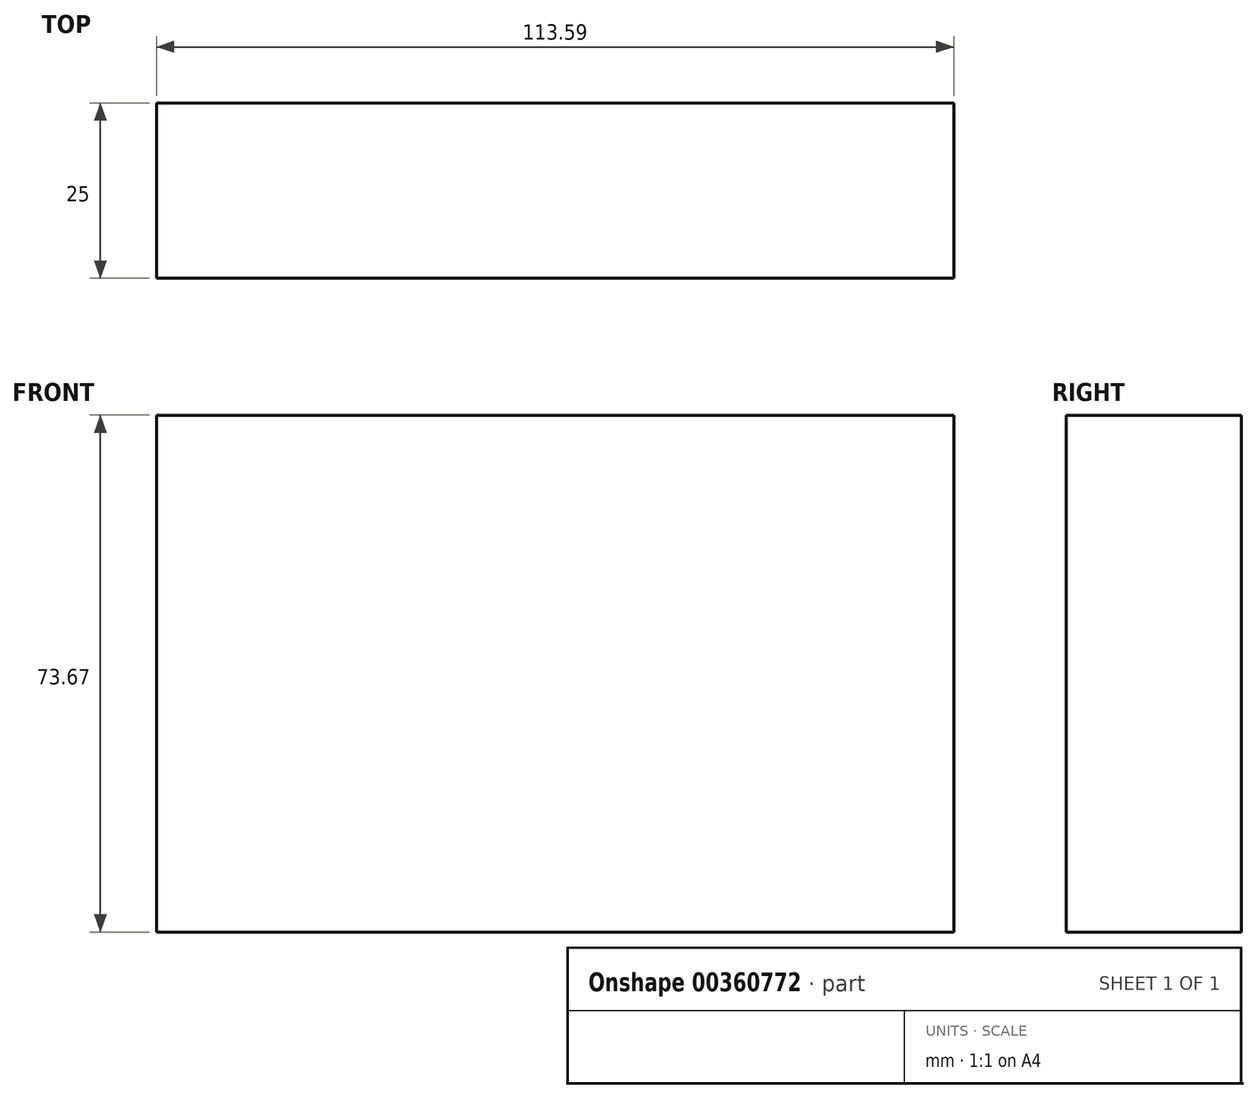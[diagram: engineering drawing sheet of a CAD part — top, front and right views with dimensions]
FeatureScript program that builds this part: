
annotation { "Feature Type Name" : "Feature", "Feature Type Description" : "" }
export const myFeature = defineFeature(function(context is Context, id is Id, definition is map)
    precondition{}
    {
        {
            var Q0;
            Q0=qCreatedBy(makeId("Front.planeOp"),FACE);
            var sketch = newSketch(context, id + "F0", { "sketchPlane" : qUnion([Q0])});
            skLineSegment(sketch, "E0.bottom", {"start": v(9.51, 4.7) * mm, "end": v(-104.08, 4.7) * mm});
            skLineSegment(sketch, "E0.top", {"start": v(9.51, 78.36) * mm, "end": v(-104.08, 78.36) * mm});
            skLineSegment(sketch, "E0.left", {"start": v(9.51, 4.7) * mm, "end": v(9.51, 78.36) * mm});
            skLineSegment(sketch, "E0.right", {"start": v(-104.08, 4.7) * mm, "end": v(-104.08, 78.36) * mm});
            skPoint(sketch, "E0.middle", {"position": v(-47.28, 41.53) * mm});
            skSolve(sketch);
        }
        {
            var Q0;
            Q0 = qSketchRegion(id + "F0", true);
            extrude(context, id + "F1", {"entities" : qUnion([Q0]), "depth" : 25 * mm});
        }
    });
